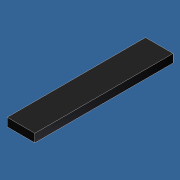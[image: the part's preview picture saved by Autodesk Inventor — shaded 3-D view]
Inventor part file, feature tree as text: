
AUTODESK INVENTOR PART (.ipt)
format: ipt  version: unknown  size: 165,888 bytes
history: native  units: mm
features: extrude x1, sketch x1
ambient origin geometry x8: Origin, YZ Plane, XZ Plane, XY Plane, X Axis, Y Axis, Z Axis, Center Point
feature tree (2):
  extrude  "Выдавливание2"  Depth=5.0mm
  sketch  "Эскиз2"
